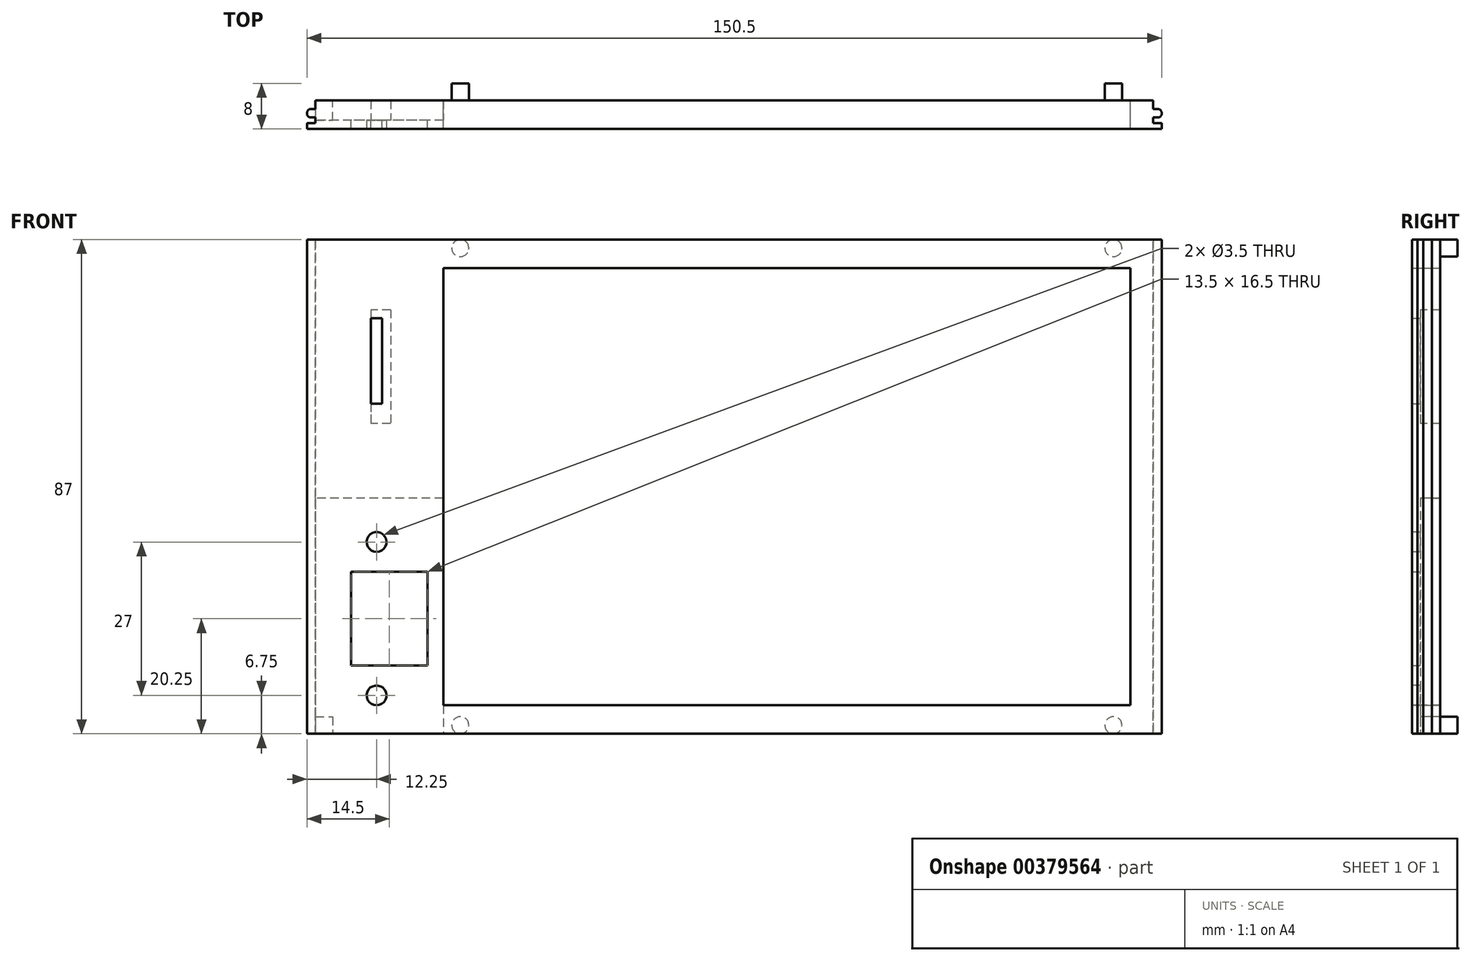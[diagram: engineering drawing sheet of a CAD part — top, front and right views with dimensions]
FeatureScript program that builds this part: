
annotation { "Feature Type Name" : "Feature", "Feature Type Description" : "" }
export const myFeature = defineFeature(function(context is Context, id is Id, definition is map)
    precondition{}
    {
        {
            var Q0;
            Q0=qCreatedBy(makeId("Front.planeOp"),FACE);
            var sketch = newSketch(context, id + "F0", { "sketchPlane" : qUnion([Q0])});
            skLineSegment(sketch, "E0.bottom", {"start": v(71.55, -42.1) * mm, "end": v(-75.95, -42.1) * mm});
            skLineSegment(sketch, "E0.top", {"start": v(71.55, 44.9) * mm, "end": v(-75.95, 44.9) * mm});
            skLineSegment(sketch, "E0.left", {"start": v(71.55, -42.1) * mm, "end": v(71.55, 44.9) * mm});
            skLineSegment(sketch, "E0.right", {"start": v(-75.95, -42.1) * mm, "end": v(-75.95, 44.9) * mm});
            skLineSegment(sketch, "E1.bottom", {"start": v(67.55, -37.1) * mm, "end": v(-53.45, -37.1) * mm});
            skLineSegment(sketch, "E1.top", {"start": v(67.55, 39.9) * mm, "end": v(-53.45, 39.9) * mm});
            skLineSegment(sketch, "E1.left", {"start": v(67.55, -37.1) * mm, "end": v(67.55, 39.9) * mm});
            skLineSegment(sketch, "E1.right", {"start": v(-53.45, -37.1) * mm, "end": v(-53.45, 39.9) * mm});
            skLineSegment(sketch, "E2.bottom", {"start": v(-69.7, -13.6) * mm, "end": v(-56.2, -13.6) * mm});
            skLineSegment(sketch, "E2.top", {"start": v(-69.7, -30.1) * mm, "end": v(-56.2, -30.1) * mm});
            skLineSegment(sketch, "E2.left", {"start": v(-69.7, -13.6) * mm, "end": v(-69.7, -30.1) * mm});
            skLineSegment(sketch, "E2.right", {"start": v(-56.2, -13.6) * mm, "end": v(-56.2, -30.1) * mm});
            skCircle(sketch, "E3", {"center": v(-65.2, -8.35) * mm, "radius": 1.75 * mm});
            skCircle(sketch, "E4.MirrorC", {"center": v(-65.2, -35.35) * mm, "radius": 1.75 * mm});
            skLineSegment(sketch, "E5", {"start": v(-65.2, 60.4) * mm, "end": v(-65.2, -47.79) * mm, "construction": true});
            skLineSegment(sketch, "E6.bottom", {"start": v(-66.2, 31.04) * mm, "end": v(-64.2, 31.04) * mm});
            skLineSegment(sketch, "E6.top", {"start": v(-66.2, 16.04) * mm, "end": v(-64.2, 16.04) * mm});
            skLineSegment(sketch, "E6.left", {"start": v(-66.2, 31.04) * mm, "end": v(-66.2, 16.04) * mm});
            skLineSegment(sketch, "E6.right", {"start": v(-64.2, 31.04) * mm, "end": v(-64.2, 16.04) * mm});
            skLineSegment(sketch, "E7", {"start": v(79.54, 43.44) * mm, "end": v(-81.76, 43.44) * mm, "construction": true});
            skSolve(sketch);
        }
        {
            var Q0;
            Q0=makeQuery(id+"F0.imprint","IMPRINT",FACE,{"disambiguationData":[TD([[makeQuery(id+"F0.imprint","IMPRINT",EDGE,{"derivedFrom":sQuery(id+"F0.wireOp",EDGE,"E0.bottom")}),-1.0]])]});
            extrude(context, id + "F1", {"entities" : qUnion([Q0]), "oppositeDirection" : true, "depth" : 5 * mm, "offsetDistance" : 25 * mm});
        }
        {
            var Q0;
            Q0=qCreatedBy(makeId("Front.planeOp"),FACE);
            var sketch = newSketch(context, id + "F2", { "sketchPlane" : qUnion([Q0])});
            skLineSegment(sketch, "E8.bottom", {"start": v(-77.45, 44.9) * mm, "end": v(73.05, 44.9) * mm});
            skLineSegment(sketch, "E8.top", {"start": v(-77.45, -42.1) * mm, "end": v(73.05, -42.1) * mm});
            skLineSegment(sketch, "E8.left", {"start": v(-77.45, 44.9) * mm, "end": v(-77.45, -42.1) * mm});
            skLineSegment(sketch, "E8.right", {"start": v(73.05, 44.9) * mm, "end": v(73.05, -42.1) * mm});
            skLineSegment(sketch, "E9.bottom", {"start": v(-69.7, -13.6) * mm, "end": v(-56.2, -13.6) * mm});
            skLineSegment(sketch, "E9.top", {"start": v(-69.7, -30.1) * mm, "end": v(-56.2, -30.1) * mm});
            skLineSegment(sketch, "E9.left", {"start": v(-69.7, -13.6) * mm, "end": v(-69.7, -30.1) * mm});
            skLineSegment(sketch, "E9.right", {"start": v(-56.2, -13.6) * mm, "end": v(-56.2, -30.1) * mm});
            skCircle(sketch, "E10", {"center": v(-65.2, -8.35) * mm, "radius": 1.75 * mm});
            skCircle(sketch, "E11.MirrorC", {"center": v(-65.2, -35.35) * mm, "radius": 1.75 * mm});
            skLineSegment(sketch, "E12.bottom", {"start": v(-66.2, 31.04) * mm, "end": v(-64.2, 31.04) * mm});
            skLineSegment(sketch, "E12.top", {"start": v(-66.2, 16.04) * mm, "end": v(-64.2, 16.04) * mm});
            skLineSegment(sketch, "E12.left", {"start": v(-66.2, 31.04) * mm, "end": v(-66.2, 16.04) * mm});
            skLineSegment(sketch, "E12.right", {"start": v(-64.2, 31.04) * mm, "end": v(-64.2, 16.04) * mm});
            skLineSegment(sketch, "E13.bottom", {"start": v(67.55, -37.1) * mm, "end": v(-53.45, -37.1) * mm});
            skLineSegment(sketch, "E13.top", {"start": v(67.55, 39.9) * mm, "end": v(-53.45, 39.9) * mm});
            skLineSegment(sketch, "E13.left", {"start": v(67.55, -37.1) * mm, "end": v(67.55, 39.9) * mm});
            skLineSegment(sketch, "E13.right", {"start": v(-53.45, -37.1) * mm, "end": v(-53.45, 39.9) * mm});
            skSolve(sketch);
        }
        {
            var Q0;
            Q0=qSketchRegion(id+"F2",true);
            extrude(context, id + "F3", {"entities" : qUnion([Q0]), "operationType" : NewBodyOperationType.ADD, "oppositeDirection" : true, "depth" : 1 * mm, "offsetDistance" : 25 * mm});
        }
        {
            var Q0;
            Q0=qCreatedBy(makeId("Front.planeOp"),FACE);
            var sketch = newSketch(context, id + "F4", { "sketchPlane" : qUnion([Q0])});
            skLineSegment(sketch, "E14.bottom", {"start": v(-53.45, -0.63) * mm, "end": v(-75.95, -0.63) * mm});
            skLineSegment(sketch, "E14.top", {"start": v(-53.45, -42.1) * mm, "end": v(-72.95, -42.1) * mm});
            skLineSegment(sketch, "E14.left", {"start": v(-53.45, -0.63) * mm, "end": v(-53.45, -42.1) * mm});
            skLineSegment(sketch, "E14.right", {"start": v(-75.95, -0.63) * mm, "end": v(-75.95, -39.1) * mm});
            skLineSegment(sketch, "E15", {"start": v(-75.95, -39.1) * mm, "end": v(-72.95, -39.1) * mm});
            skLineSegment(sketch, "E16", {"start": v(-72.95, -39.1) * mm, "end": v(-72.95, -42.1) * mm});
            skSolve(sketch);
        }
        {
            var Q0;
            Q0=qCreatedBy(makeId("Front.planeOp"),FACE);
            var sketch = newSketch(context, id + "F5", { "sketchPlane" : qUnion([Q0])});
            skLineSegment(sketch, "E17.bottom", {"start": v(-62.7, 32.54) * mm, "end": v(-66.2, 32.54) * mm});
            skLineSegment(sketch, "E17.top", {"start": v(-62.7, 12.54) * mm, "end": v(-66.2, 12.54) * mm});
            skLineSegment(sketch, "E17.left", {"start": v(-62.7, 32.54) * mm, "end": v(-62.7, 12.54) * mm});
            skLineSegment(sketch, "E17.right", {"start": v(-66.2, 32.54) * mm, "end": v(-66.2, 12.54) * mm});
            skSolve(sketch);
        }
        {
            var Q0;
            Q0=qSketchRegion(id+"F2",true);
            extrude(context, id + "F6", {"entities" : qUnion([Q0]), "operationType" : NewBodyOperationType.ADD, "oppositeDirection" : true, "depth" : 3.5 * mm, "offsetDistance" : 25 * mm, "hasSecondDirection" : true, "secondDirectionOppositeDirection" : true, "secondDirectionDepth" : 2 * mm});
        }
        {
            var Q0;
            Q0=qSketchRegion(id+"F5",true);
            extrude(context, id + "F7", {"entities" : qUnion([Q0]), "operationType" : NewBodyOperationType.REMOVE, "oppositeDirection" : true, "depth" : 22 * mm, "offsetDistance" : 25 * mm, "hasSecondDirection" : true, "secondDirectionOppositeDirection" : true, "secondDirectionDepth" : 1.5 * mm});
        }
        {
            var Q0;
            Q0=qSketchRegion(id+"F4",true);
            extrude(context, id + "F8", {"entities" : qUnion([Q0]), "operationType" : NewBodyOperationType.REMOVE, "oppositeDirection" : true, "depth" : 22 * mm, "offsetDistance" : 25 * mm, "hasSecondDirection" : true, "secondDirectionOppositeDirection" : true, "secondDirectionDepth" : 1.5 * mm});
        }
        {
            var Q0;
            Q0=qCreatedBy(makeId("Front.planeOp"),FACE);
            var sketch = newSketch(context, id + "F9", { "sketchPlane" : qUnion([Q0])});
            skLineSegment(sketch, "E18", {"start": v(64.55, 57) * mm, "end": v(64.55, -54.93) * mm, "construction": true});
            skLineSegment(sketch, "E19", {"start": v(-50.45, 54.3) * mm, "end": v(-50.45, -55.44) * mm, "construction": true});
            skLineSegment(sketch, "E20", {"start": v(80.65, 43.4) * mm, "end": v(-83.14, 43.4) * mm, "construction": true});
            skLineSegment(sketch, "E21", {"start": v(80.9, -40.6) * mm, "end": v(-82.9, -40.6) * mm, "construction": true});
            skCircle(sketch, "E22", {"center": v(64.55, 43.4) * mm, "radius": 1.5 * mm});
            skCircle(sketch, "E23", {"center": v(64.55, -40.6) * mm, "radius": 1.5 * mm});
            skCircle(sketch, "E24", {"center": v(-50.45, -40.6) * mm, "radius": 1.5 * mm});
            skCircle(sketch, "E25", {"center": v(-50.45, 43.4) * mm, "radius": 1.5 * mm});
            skSolve(sketch);
        }
        {
            var Q0;
            Q0=qSketchRegion(id+"F9",true);
            extrude(context, id + "F10", {"entities" : qUnion([Q0]), "operationType" : NewBodyOperationType.ADD, "oppositeDirection" : true, "depth" : 8 * mm, "offsetDistance" : 25 * mm});
        }
        {
            var Q0;
            Q0=makeQuery(id+"F6.opExtrude","CAP_EDGE",EDGE,{"disambiguationData":[OSD([sQuery(id+"F2.wireOp",EDGE,"E8.right")])],"isStart":true});
            fillet(context, id + "F11", {"entities" : qUnion([Q0]), "radius" : 0.7 * mm, "allowEdgeOverflow" : false});
        }
        {
            var Q0;
            Q0=makeQuery(id+"F6.opExtrude","CAP_EDGE",EDGE,{"disambiguationData":[OSD([sQuery(id+"F2.wireOp",EDGE,"E8.left")])],"isStart":true});
            fillet(context, id + "F12", {"entities" : qUnion([Q0]), "radius" : 0.7 * mm, "tangentPropagation" : true, "allowEdgeOverflow" : false});
        }
        {
            var Q0;
            Q0=makeQuery(id+"F6.opExtrude","CAP_EDGE",EDGE,{"disambiguationData":[OSD([sQuery(id+"F2.wireOp",EDGE,"E8.right")])],"isStart":false});
            fillet(context, id + "F13", {"entities" : qUnion([Q0]), "radius" : 0.7 * mm, "tangentPropagation" : true, "allowEdgeOverflow" : false});
        }
        {
            var Q0;
            Q0=makeQuery(id+"F6.opExtrude","CAP_EDGE",EDGE,{"disambiguationData":[OSD([sQuery(id+"F2.wireOp",EDGE,"E8.left")])],"isStart":false});
            fillet(context, id + "F14", {"entities" : qUnion([Q0]), "radius" : 0.7 * mm, "tangentPropagation" : true, "allowEdgeOverflow" : false});
        }
    });
